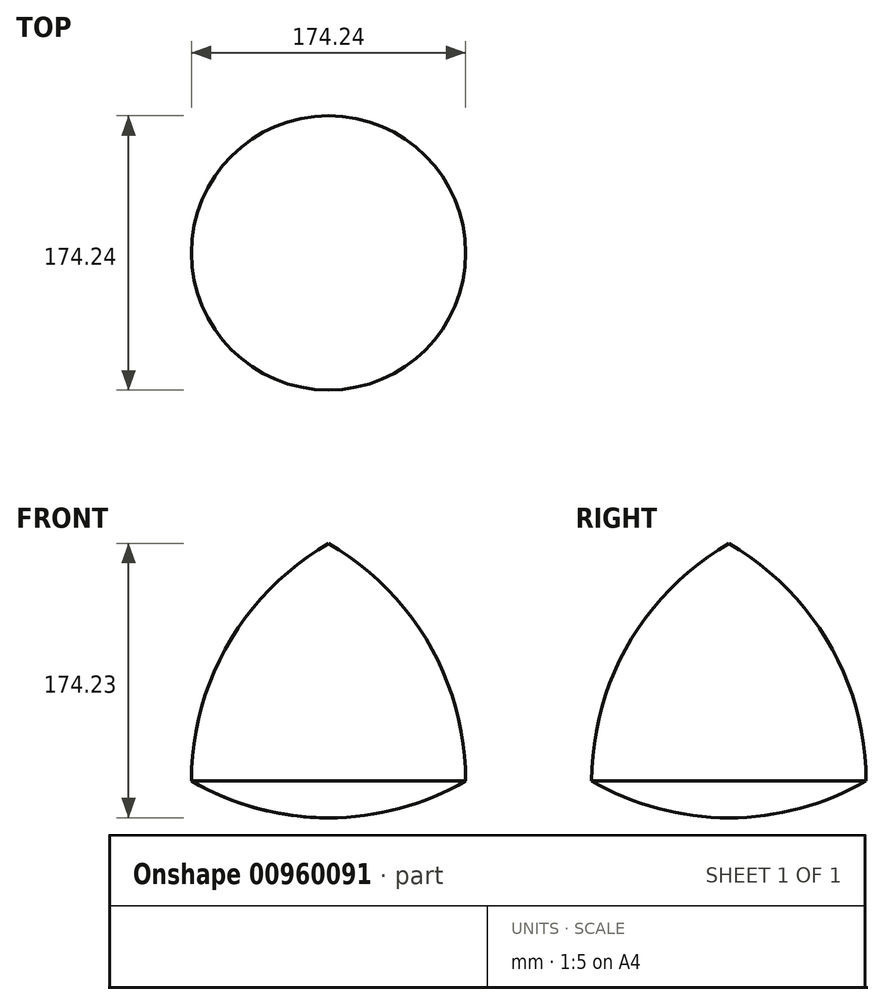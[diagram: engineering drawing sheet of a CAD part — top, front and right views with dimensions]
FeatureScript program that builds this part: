
annotation { "Feature Type Name" : "Feature", "Feature Type Description" : "" }
export const myFeature = defineFeature(function(context is Context, id is Id, definition is map)
    precondition{}
    {
        {
            var Q0;
            Q0=qCreatedBy(makeId("Front.planeOp"),FACE);
            var sketch = newSketch(context, id + "F0", { "sketchPlane" : qUnion([Q0])});
            skCircle(sketch, "E0.cCircle", {"center": v(0, 0) * mm, "radius": 50.3 * mm, "construction": true});
            skLineSegment(sketch, "E0.0", {"start": v(87.12, -50.3) * mm, "end": v(-87.12, -50.3) * mm});
            skLineSegment(sketch, "E0.1", {"start": v(-87.12, -50.3) * mm, "end": v(0, 100.6) * mm});
            skLineSegment(sketch, "E0.2", {"start": v(0, 100.6) * mm, "end": v(87.12, -50.3) * mm});
            skPoint(sketch, "E0.0.midPoint", {"position": v(0, -50.3) * mm});
            skLineSegment(sketch, "E1", {"start": v(0, 100.6) * mm, "end": v(0, -50.3) * mm});
            skArc(sketch, "E2", {"start": v(-87.12, -50.3) * mm, "mid": v(0, -73.64) * mm, "end": v(87.12, -50.3) * mm});
            skArc(sketch, "E3", {"start": v(0, 100.6) * mm, "mid": v(-63.77, 36.82) * mm, "end": v(-87.12, -50.3) * mm});
            skArc(sketch, "E4.trimOffspring", {"start": v(87.12, -50.3) * mm, "mid": v(63.77, 36.82) * mm, "end": v(0, 100.6) * mm});
            skLineSegment(sketch, "E5", {"start": v(0, -50.3) * mm, "end": v(0, -73.64) * mm});
            skLineSegment(sketch, "E6", {"start": v(0, 100.6) * mm, "end": v(0, -73.64) * mm, "construction": true});
            skSolve(sketch);
        }
        {
            var Q0;
            {var subQ0=sQuery(id+"F0.wireOp",EDGE,"E0.1");Q0=makeQuery(id+"F0.imprint","IMPRINT",FACE,{"disambiguationData":[TD([[makeQuery(id+"F0.imprint","IMPRINT",EDGE,{"derivedFrom":subQ0}),-1.0]])]});}
            var Q1;
            Q1=makeQuery(id+"F0.imprint","IMPRINT",FACE,{"disambiguationData":[TD([[makeQuery(id+"F0.imprint","IMPRINT",EDGE,{"derivedFrom":sQuery(id+"F0.wireOp",EDGE,"E0.1")}),1.0]])]});
            var Q2;
            {var subQ3=sQuery(id+"F0.wireOp",EDGE,"E5");Q2=makeQuery(id+"F0.imprint","IMPRINT",FACE,{"disambiguationData":[TD([[makeQuery(id+"F0.imprint","IMPRINT",EDGE,{"derivedFrom":subQ3}),-1.0]])]});}
            var Q3;
            Q3=sQuery(id+"F0.wireOp",EDGE,"E1");
            revolve(context, id + "F1", {"surfaceOperationType" : NewSurfaceOperationType.NEW, "entities" : qUnion([Q0, Q1, Q2]), "axis" : qUnion([Q3]), "revolveType" : RevolveType.FULL});
        }
    });
